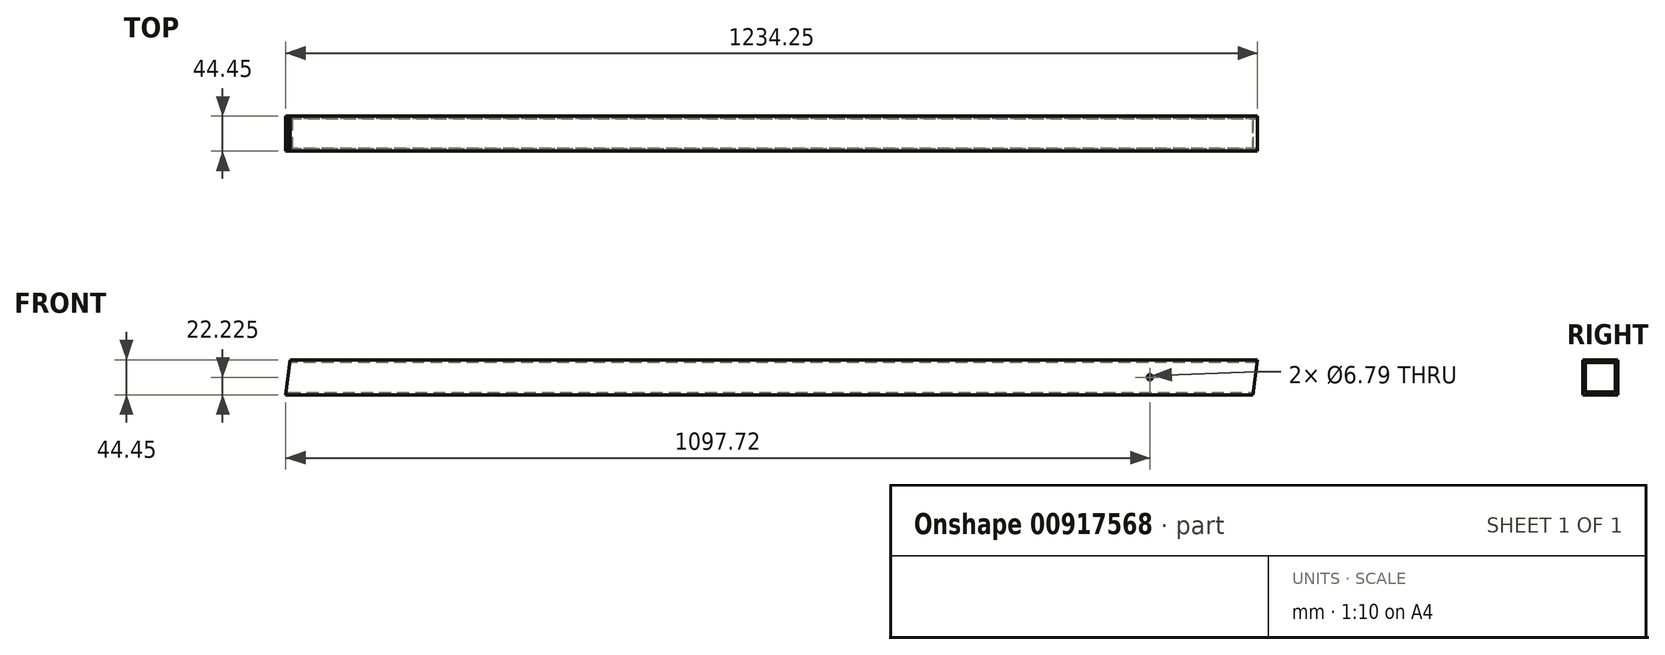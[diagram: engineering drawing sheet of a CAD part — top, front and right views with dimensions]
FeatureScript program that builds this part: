
annotation { "Feature Type Name" : "Feature", "Feature Type Description" : "" }
export const myFeature = defineFeature(function(context is Context, id is Id, definition is map)
    precondition{}
    {
        {
            var Q0;
            Q0=qCreatedBy(makeId("Front.planeOp"),FACE);
            var sketch = newSketch(context, id + "F0", { "sketchPlane" : qUnion([Q0])});
            skLineSegment(sketch, "E0", {"start": v(17.97, -44.45) * mm, "end": v(1223.13, -44.45) * mm});
            skLineSegment(sketch, "E1", {"start": v(1223.13, -44.45) * mm, "end": v(1228.69, 0) * mm});
            skLineSegment(sketch, "E2", {"start": v(1228.69, 0) * mm, "end": v(0, 0) * mm});
            skLineSegment(sketch, "E3", {"start": v(0, 0) * mm, "end": v(-5.56, -44.45) * mm});
            skLineSegment(sketch, "E4", {"start": v(-5.56, -44.45) * mm, "end": v(17.97, -44.45) * mm});
            skSolve(sketch);
        }
        {
            var Q0;
            Q0=makeQuery(id+"F0.imprint","IMPRINT",FACE,{"disambiguationData":[TD([[makeQuery(id+"F0.imprint","IMPRINT",EDGE,{"derivedFrom":sQuery(id+"F0.wireOp",EDGE,"E0")}),1.0]])]});
            extrude(context, id + "F1", {"entities" : qUnion([Q0]), "depth" : 44.45 * mm, "offsetDistance" : 25.4 * mm});
        }
        {
            var Q0;
            Q0=makeQuery(id+"F1.opExtrude","SWEPT_FACE",FACE,{"disambiguationData":[OSD([sQuery(id+"F0.wireOp",EDGE,"E1")])]});
            shell(context, id + "F2", {"entities" : qUnion([Q0]), "thickness" : 3.17 * mm});
        }
        {
            var Q0;
            Q0=makeQuery(id+"F2.opShell","OFFSET_FACE",FACE,{"disambiguationData":[OSD([sQuery(id+"F0.wireOp",EDGE,"E3")])]});
            var sketch = newSketch(context, id + "F3", { "sketchPlane" : qUnion([Q0])});
            skSolve(sketch);
        }
        {
            var Q0;
            {var subQ0=sQuery(id+"F0.wireOp",EDGE,"E3");Q0=makeQuery(id+"F3.imprint","IMPRINT",FACE,{"disambiguationData":[TD([[makeQuery(id+"F3.imprint","IMPRINT",EDGE,{"derivedFrom":makeQuery(id+"F2.opShell","OFFSET_EDGE",EDGE,{"disambiguationData":[OSD([subQ0]),TDD([makeQuery(id+"F1.opExtrude","CAP_EDGE",EDGE,{"disambiguationData":[OSD([subQ0])],"isStart":true})])]})}),-1.0]])]});}
            extrude(context, id + "F4", {"entities" : qUnion([Q0]), "operationType" : NewBodyOperationType.REMOVE, "endBound" : BoundingType.THROUGH_ALL, "oppositeDirection" : true, "depth" : 25.4 * mm, "offsetDistance" : 25.4 * mm});
        }
        {
            var Q0;
            Q0=makeQuery(id+"F1.opExtrude","CAP_FACE",FACE,{"disambiguationData":[OSD([sQuery(id+"F0.wireOp",EDGE,"E0"),sQuery(id+"F0.wireOp",EDGE,"E1"),sQuery(id+"F0.wireOp",EDGE,"E2"),sQuery(id+"F0.wireOp",EDGE,"E3"),sQuery(id+"F0.wireOp",EDGE,"E4")])],"isStart":false});
            var sketch = newSketch(context, id + "F5", { "sketchPlane" : qUnion([Q0])});
            skPoint(sketch, "E5", {"position": v(1092.16, -22.23) * mm});
            skSolve(sketch);
        }
        {
            var Q0;
            Q0=sQuery(id+"F5.wireOp",VERTEX,"E5");
            var Q1;
            Q1=makeQuery(id+"F1.opExtrude","SWEPT_BODY",BODY,{"disambiguationData":[OSD([sQuery(id+"F0.wireOp",EDGE,"E0"),sQuery(id+"F0.wireOp",EDGE,"E1"),sQuery(id+"F0.wireOp",EDGE,"E2"),sQuery(id+"F0.wireOp",EDGE,"E3"),sQuery(id+"F0.wireOp",EDGE,"E4")])]});
            hole(context, id + "F6", {"style" : HoleStyle.SIMPLE, "endStyle" : HoleEndStyle.THROUGH, "holeDiameter" : 6.8 * mm, "majorDiameter" : 6.35 * mm, "isTappedThrough" : true, "tappedDepth" : 12.7 * mm, "tapClearance" : 3, "locations" : qUnion([Q0]), "scope" : qUnion([Q1])});
        }
    });
